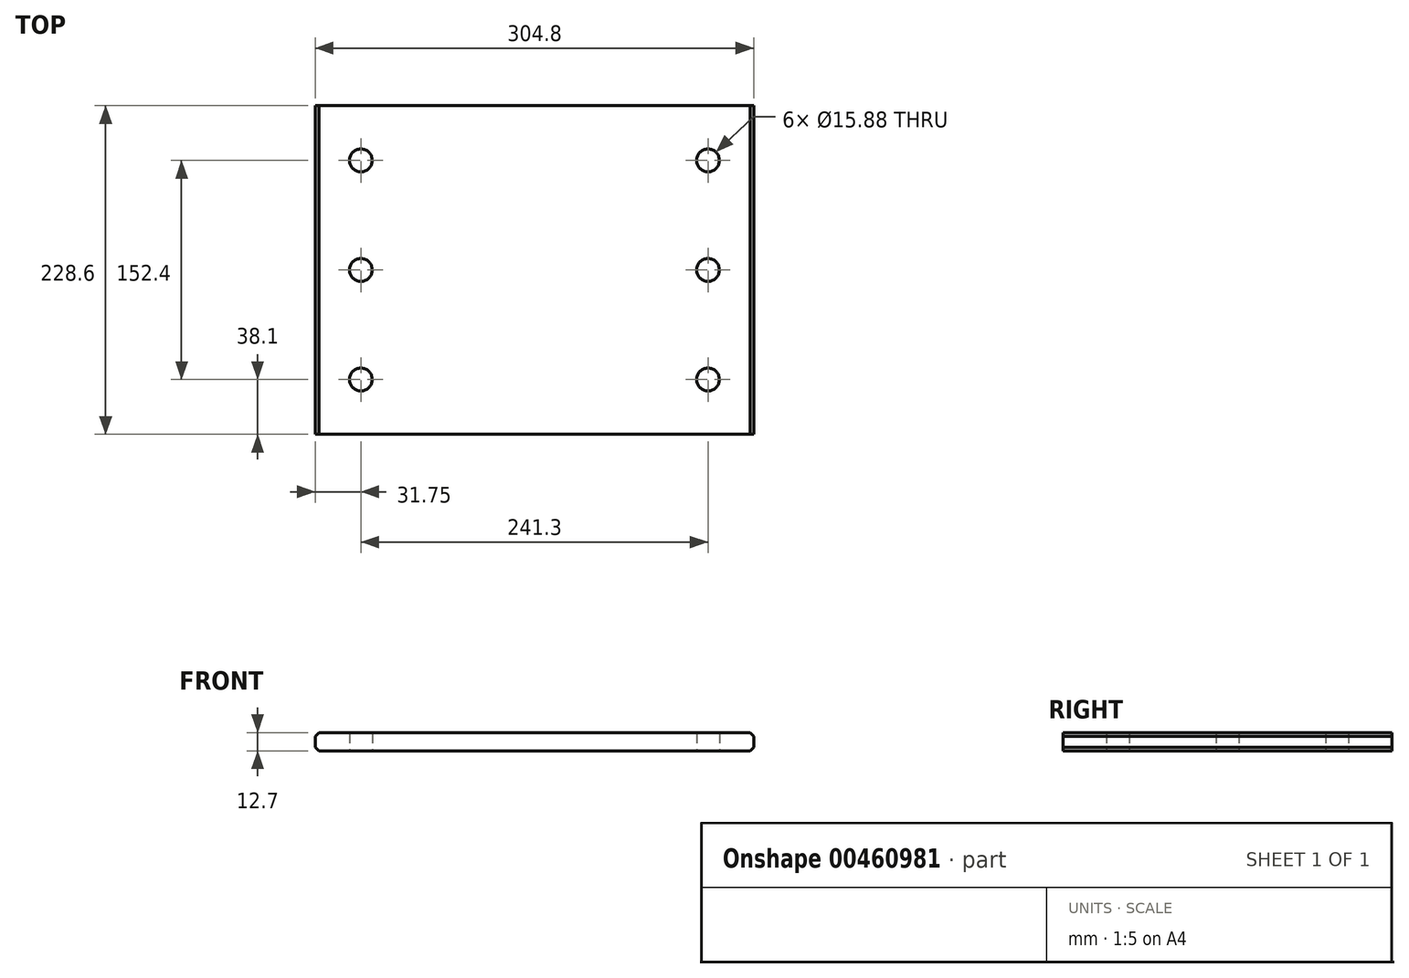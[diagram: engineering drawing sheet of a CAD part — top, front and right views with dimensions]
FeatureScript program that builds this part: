
annotation { "Feature Type Name" : "Feature", "Feature Type Description" : "" }
export const myFeature = defineFeature(function(context is Context, id is Id, definition is map)
    precondition{}
    {
        {
            var Q0;
            Q0=qCreatedBy(makeId("Top.planeOp"),FACE);
            var sketch = newSketch(context, id + "F0", { "sketchPlane" : qUnion([Q0])});
            skLineSegment(sketch, "E0.bottom", {"start": v(-152.4, 114.3) * mm, "end": v(152.4, 114.3) * mm});
            skLineSegment(sketch, "E0.top", {"start": v(-152.4, -114.3) * mm, "end": v(152.4, -114.3) * mm});
            skLineSegment(sketch, "E0.left", {"start": v(-152.4, 114.3) * mm, "end": v(-152.4, -114.3) * mm});
            skLineSegment(sketch, "E0.right", {"start": v(152.4, 114.3) * mm, "end": v(152.4, -114.3) * mm});
            skPoint(sketch, "E0.middle", {"position": v(0, 0) * mm});
            skCircle(sketch, "E1", {"center": v(-120.65, 0) * mm, "radius": 7.94 * mm});
            skCircle(sketch, "E2.MirrorC", {"center": v(-120.65, 76.2) * mm, "radius": 7.94 * mm});
            skCircle(sketch, "E3.MirrorC", {"center": v(-120.65, -76.2) * mm, "radius": 7.94 * mm});
            skCircle(sketch, "E4.MirrorC", {"center": v(120.65, 76.2) * mm, "radius": 7.94 * mm});
            skCircle(sketch, "E5.MirrorC", {"center": v(120.65, 0) * mm, "radius": 7.94 * mm});
            skCircle(sketch, "E6.MirrorC", {"center": v(120.65, -76.2) * mm, "radius": 7.94 * mm});
            skSolve(sketch);
        }
        {
            var Q0;
            Q0=makeQuery(id+"F0.imprint","IMPRINT",FACE,{"disambiguationData":[TD([[makeQuery(id+"F0.imprint","IMPRINT",EDGE,{"derivedFrom":sQuery(id+"F0.wireOp",EDGE,"E0.top")}),1.0]])]});
            extrude(context, id + "F1", {"entities" : qUnion([Q0]), "depth" : 12.7 * mm, "offsetDistance" : 25.4 * mm});
        }
        {
            var Q0;
            Q0=makeQuery(id+"F1.opExtrude","CAP_EDGE",EDGE,{"disambiguationData":[OSD([sQuery(id+"F0.wireOp",EDGE,"E0.left")])],"isStart":false});
            var Q1;
            Q1=makeQuery(id+"F1.opExtrude","CAP_EDGE",EDGE,{"disambiguationData":[OSD([sQuery(id+"F0.wireOp",EDGE,"E0.left")])],"isStart":true});
            var Q2;
            Q2=makeQuery(id+"F1.opExtrude","CAP_EDGE",EDGE,{"disambiguationData":[OSD([sQuery(id+"F0.wireOp",EDGE,"E0.right")])],"isStart":true});
            var Q3;
            Q3=makeQuery(id+"F1.opExtrude","CAP_EDGE",EDGE,{"disambiguationData":[OSD([sQuery(id+"F0.wireOp",EDGE,"E0.right")])],"isStart":false});
            chamfer(context, id + "F2", {"entities" : qUnion([Q0, Q1, Q2, Q3]), "width" : 2.54 * mm, "tangentPropagation" : true});
        }
    });
